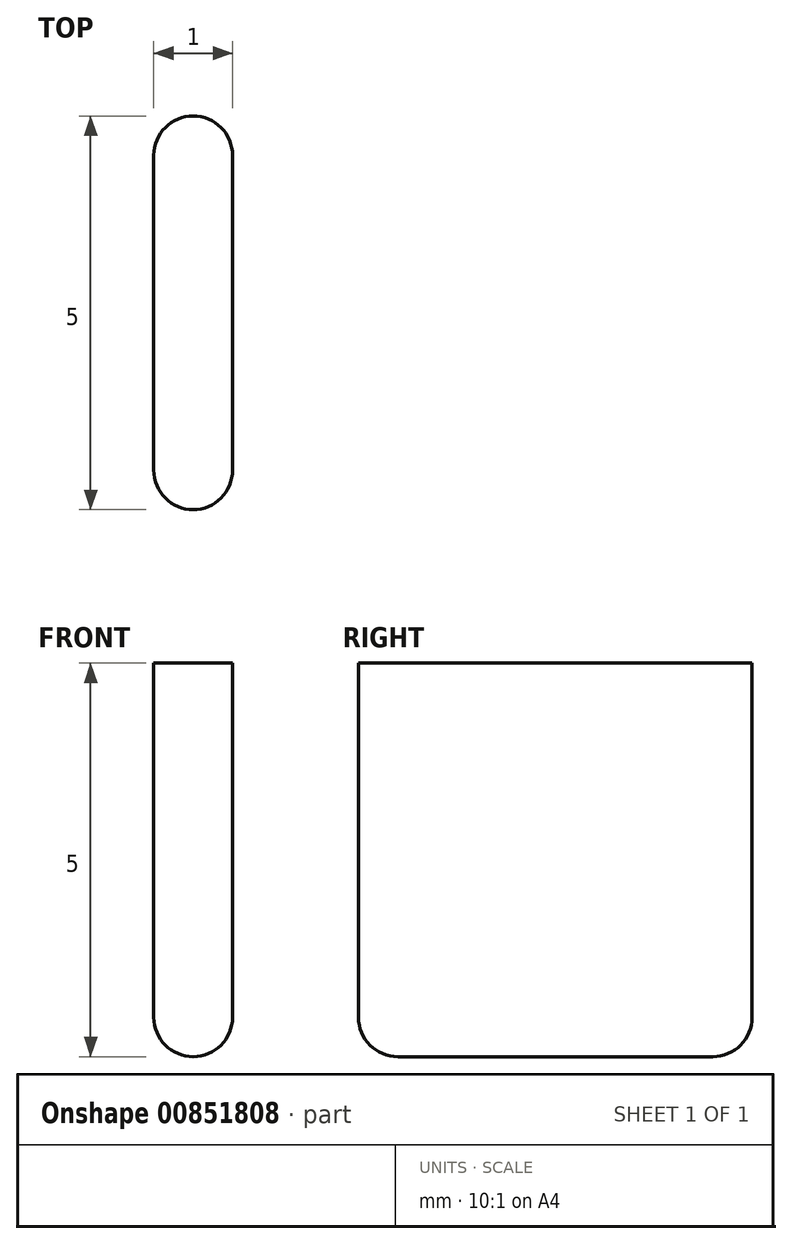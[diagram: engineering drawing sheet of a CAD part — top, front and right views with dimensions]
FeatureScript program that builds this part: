
annotation { "Feature Type Name" : "Feature", "Feature Type Description" : "" }
export const myFeature = defineFeature(function(context is Context, id is Id, definition is map)
    precondition{}
    {
        {
            var Q0;
            Q0=qCreatedBy(makeId("Top.planeOp"),FACE);
            var sketch = newSketch(context, id + "F0", { "sketchPlane" : qUnion([Q0])});
            skLineSegment(sketch, "E0.bottom", {"start": v(-0.5, 2.5) * mm, "end": v(0.5, 2.5) * mm});
            skLineSegment(sketch, "E0.top", {"start": v(-0.5, -2.5) * mm, "end": v(0.5, -2.5) * mm});
            skLineSegment(sketch, "E0.left", {"start": v(-0.5, 2.5) * mm, "end": v(-0.5, -2.5) * mm});
            skLineSegment(sketch, "E0.right", {"start": v(0.5, 2.5) * mm, "end": v(0.5, -2.5) * mm});
            skPoint(sketch, "E0.middle", {"position": v(0, 0) * mm});
            skSolve(sketch);
        }
        {
            var Q0;
            Q0=makeQuery(id+"F0.imprint","IMPRINT",FACE,{"disambiguationData":[TD([[makeQuery(id+"F0.imprint","IMPRINT",EDGE,{"derivedFrom":sQuery(id+"F0.wireOp",EDGE,"E0.bottom")}),-1.0]])]});
            extrude(context, id + "F1", {"entities" : qUnion([Q0]), "depth" : 5 * mm, "offsetDistance" : 25.4 * mm});
        }
        {
            var Q0;
            Q0=makeQuery(id+"F1.opExtrude","CAP_FACE",FACE,{"disambiguationData":[OSD([sQuery(id+"F0.wireOp",EDGE,"E0.bottom"),sQuery(id+"F0.wireOp",EDGE,"E0.top"),sQuery(id+"F0.wireOp",EDGE,"E0.left"),sQuery(id+"F0.wireOp",EDGE,"E0.right")])],"isStart":true});
            var Q1;
            Q1=makeQuery(id+"F1.opExtrude","SWEPT_EDGE",EDGE,{"disambiguationData":[OSD([sQuery(id+"F0.wireOp",EDGE,"E0.bottom"),sQuery(id+"F0.wireOp",EDGE,"E0.right")])]});
            var Q2;
            Q2=makeQuery(id+"F1.opExtrude","SWEPT_EDGE",EDGE,{"disambiguationData":[OSD([sQuery(id+"F0.wireOp",EDGE,"E0.bottom"),sQuery(id+"F0.wireOp",EDGE,"E0.left")])]});
            var Q3;
            Q3=makeQuery(id+"F1.opExtrude","SWEPT_EDGE",EDGE,{"disambiguationData":[OSD([sQuery(id+"F0.wireOp",EDGE,"E0.top"),sQuery(id+"F0.wireOp",EDGE,"E0.left")])]});
            var Q4;
            Q4=makeQuery(id+"F1.opExtrude","SWEPT_EDGE",EDGE,{"disambiguationData":[OSD([sQuery(id+"F0.wireOp",EDGE,"E0.top"),sQuery(id+"F0.wireOp",EDGE,"E0.right")])]});
            fillet(context, id + "F2", {"entities" : qUnion([Q0, Q1, Q2, Q3, Q4]), "radius" : .5 * mm, "tangentPropagation" : true, "allowEdgeOverflow" : false});
        }
    });
